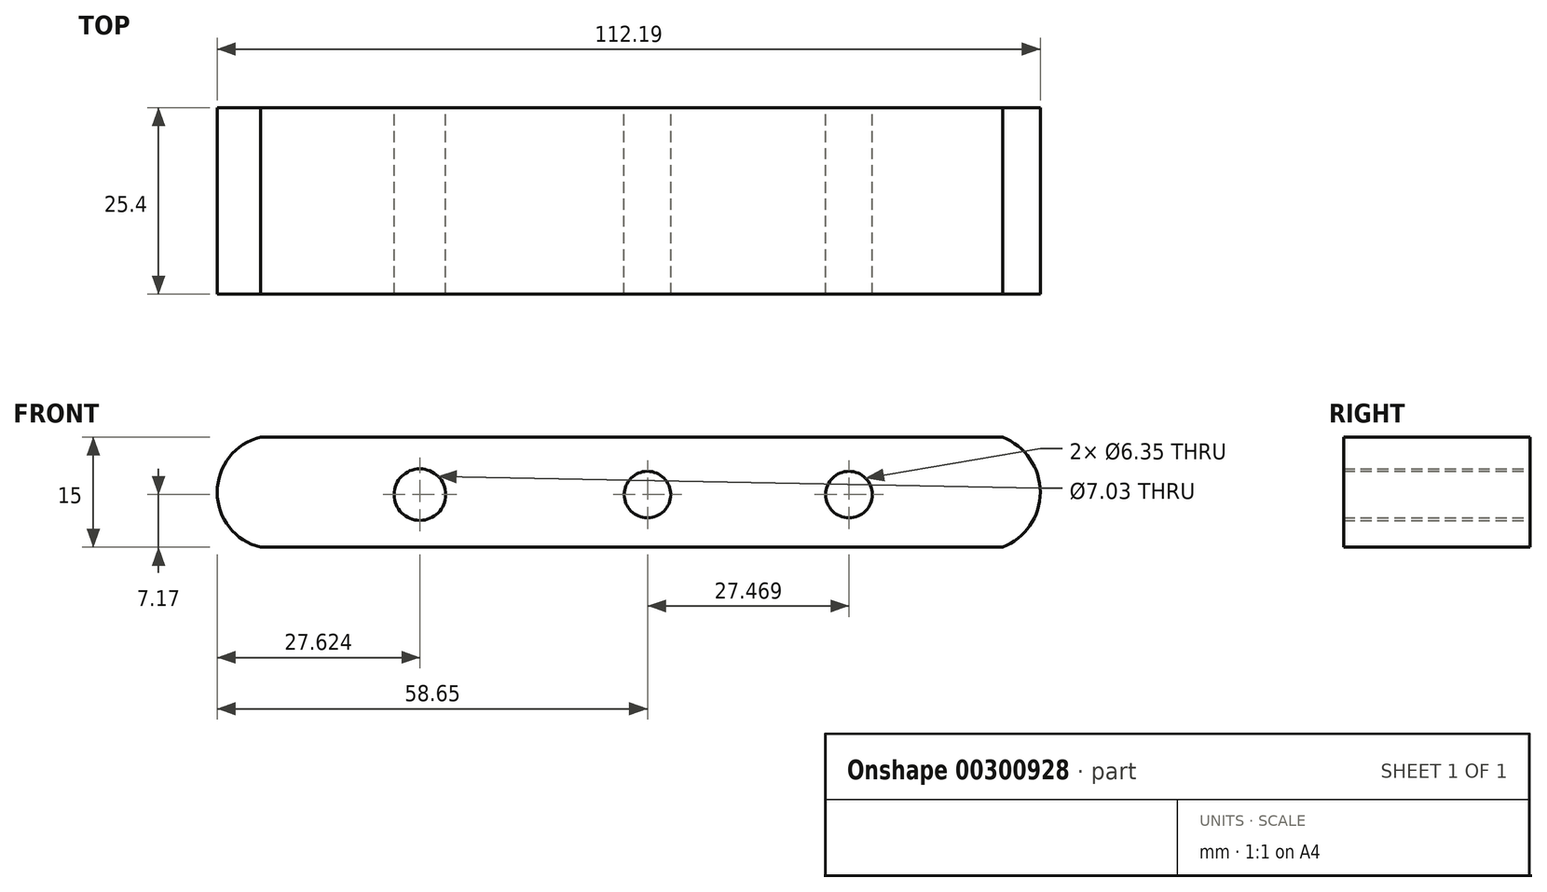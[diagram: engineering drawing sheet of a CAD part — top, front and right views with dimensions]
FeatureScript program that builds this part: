
annotation { "Feature Type Name" : "Feature", "Feature Type Description" : "" }
export const myFeature = defineFeature(function(context is Context, id is Id, definition is map)
    precondition{}
    {
        {
            var Q0;
            Q0=qCreatedBy(makeId("Front.planeOp"),FACE);
            var sketch = newSketch(context, id + "F0", { "sketchPlane" : qUnion([Q0])});
            skLineSegment(sketch, "E0.bottom", {"start": v(-52.72, 7.83) * mm, "end": v(48.4, 7.83) * mm});
            skLineSegment(sketch, "E0.top", {"start": v(-52.72, -7.17) * mm, "end": v(48.4, -7.17) * mm});
            skLineSegment(sketch, "E0.left", {"start": v(-52.72, 7.83) * mm, "end": v(-52.72, -7.17) * mm});
            skLineSegment(sketch, "E0.right", {"start": v(48.4, 7.83) * mm, "end": v(48.4, -7.17) * mm});
            skCircle(sketch, "E1", {"center": v(-31.03, 0) * mm, "radius": 3.51 * mm});
            skPoint(sketch, "E2", {"position": v(48.4, 0.33) * mm});
            skCircle(sketch, "E3", {"center": v(27.47, 0) * mm, "radius": 3.17 * mm});
            skCircle(sketch, "E4", {"center": v(0, 0) * mm, "radius": 3.17 * mm});
            skArc(sketch, "E5", {"start": v(48.4, -7.17) * mm, "mid": v(53.54, 0.33) * mm, "end": v(48.4, 7.83) * mm});
            skArc(sketch, "E6", {"start": v(-52.72, 7.83) * mm, "mid": v(-58.65, 0.33) * mm, "end": v(-52.72, -7.17) * mm});
            skSolve(sketch);
        }
        {
            var Q0;
            Q0 = qSketchRegion(id + "F0", true);
            extrude(context, id + "F1", {"entities" : qUnion([Q0]), "depth" : 25.4 * mm});
        }
    });
